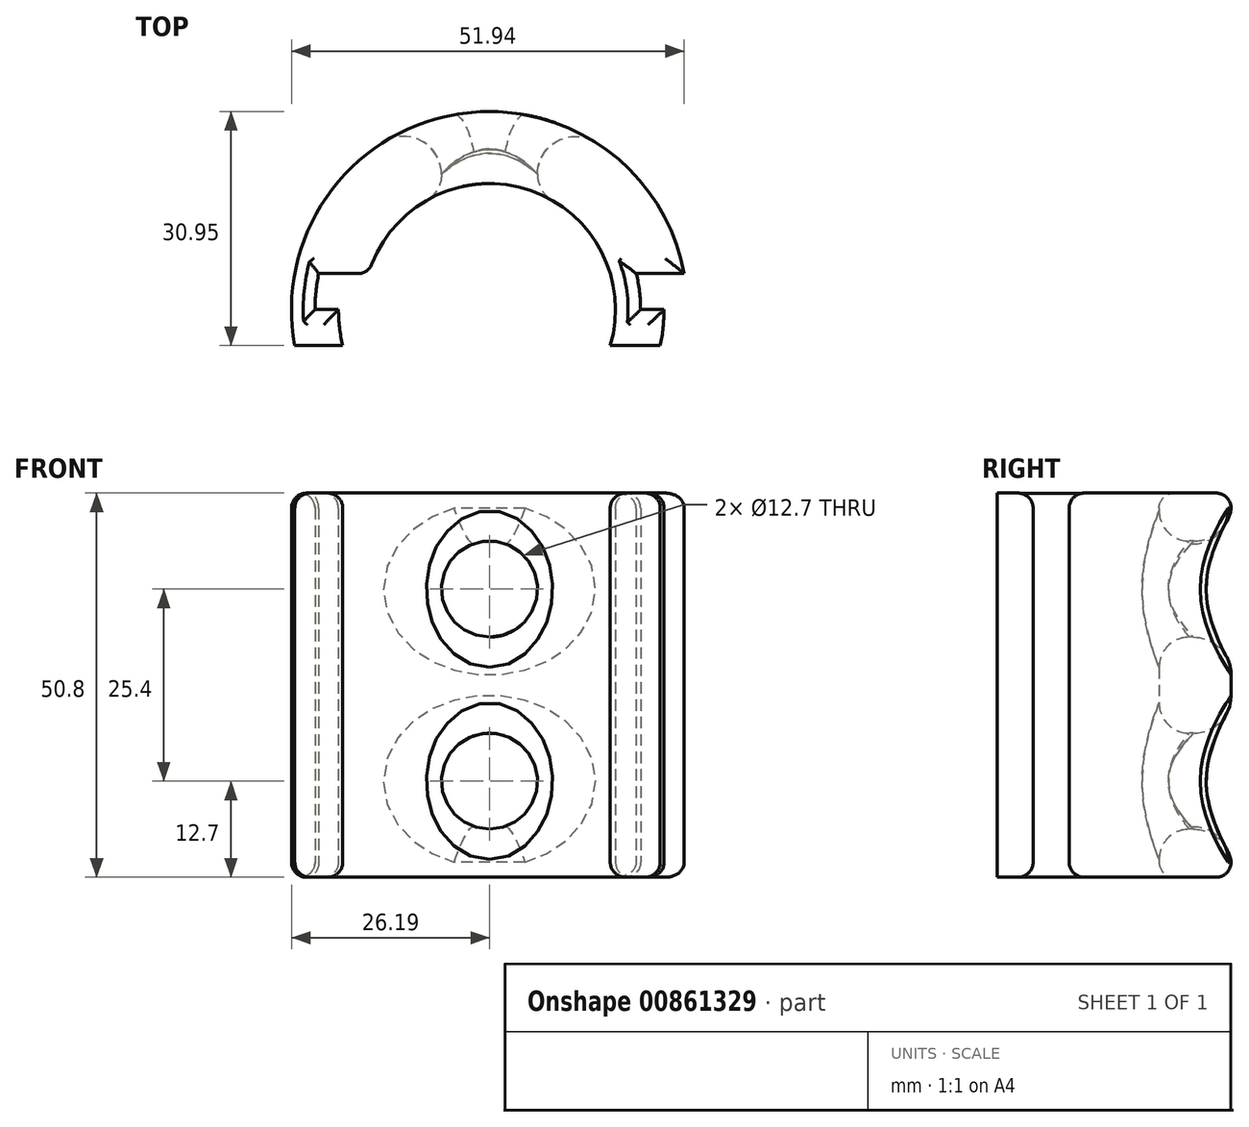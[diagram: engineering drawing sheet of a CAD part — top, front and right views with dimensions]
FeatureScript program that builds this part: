
annotation { "Feature Type Name" : "Feature", "Feature Type Description" : "" }
export const myFeature = defineFeature(function(context is Context, id is Id, definition is map)
    precondition{}
    {
        {
            var Q0;
            Q0=qCreatedBy(makeId("Top.planeOp"),FACE);
            var sketch = newSketch(context, id + "F0", { "sketchPlane" : qUnion([Q0])});
            skArc(sketch, "E0", {"start": v(15.96, -4.76) * mm, "mid": v(4.76, 15.96) * mm, "end": v(-15.96, 4.76) * mm});
            skArc(sketch, "E1", {"start": v(25.75, 4.76) * mm, "mid": v(-4.76, 25.75) * mm, "end": v(-25.75, -4.76) * mm});
            skLineSegment(sketch, "E2.top", {"start": v(-25.75, -4.76) * mm, "end": v(-19.4, -4.76) * mm, "construction": true});
            skLineSegment(sketch, "E3", {"start": v(-25.75, -4.76) * mm, "end": v(-19.4, -4.76) * mm});
            skArc(sketch, "E4", {"start": v(-19.97, 0) * mm, "mid": v(-19.83, -2.4) * mm, "end": v(-19.4, -4.76) * mm});
            skLineSegment(sketch, "E5", {"start": v(-25.75, -4.76) * mm, "end": v(-22.57, -4.76) * mm, "construction": true});
            skArc(sketch, "E6", {"start": v(22.57, -4.76) * mm, "mid": v(22.95, -2.4) * mm, "end": v(23.07, 0) * mm});
            skLineSegment(sketch, "E7", {"start": v(-19.97, 0) * mm, "end": v(-23.07, 0) * mm});
            skLineSegment(sketch, "E8", {"start": v(-22.57, 4.76) * mm, "end": v(-15.96, 4.76) * mm});
            skArc(sketch, "E9.trimOffspring", {"start": v(-22.57, 4.76) * mm, "mid": v(-22.95, 2.4) * mm, "end": v(-23.07, 0) * mm});
            skArc(sketch, "E10.trimOffspring", {"start": v(19.97, 0) * mm, "mid": v(19.83, 2.4) * mm, "end": v(19.4, 4.76) * mm});
            skLineSegment(sketch, "E11", {"start": v(15.96, -4.76) * mm, "end": v(22.57, -4.76) * mm});
            skLineSegment(sketch, "E12", {"start": v(23.07, 0) * mm, "end": v(19.97, 0) * mm});
            skLineSegment(sketch, "E13", {"start": v(19.4, 4.76) * mm, "end": v(25.75, 4.76) * mm});
            skLineSegment(sketch, "E14.trimOffspring", {"start": v(15.96, -4.76) * mm, "end": v(22.57, -4.76) * mm, "construction": true});
            skLineSegment(sketch, "E15.trimOffspring", {"start": v(19.4, 4.76) * mm, "end": v(25.75, 4.76) * mm, "construction": true});
            skLineSegment(sketch, "E16.trimOffspring", {"start": v(-22.57, 4.76) * mm, "end": v(-15.96, 4.76) * mm, "construction": true});
            skSolve(sketch);
        }
        {
            var Q0;
            Q0=makeQuery(id+"F0.imprint","IMPRINT",FACE,{"disambiguationData":[TD([[makeQuery(id+"F0.imprint","IMPRINT",EDGE,{"derivedFrom":sQuery(id+"F0.wireOp",EDGE,"E0")}),-1.0]])]});
            extrude(context, id + "F1", {"entities" : qUnion([Q0]), "depth" : 50.8 * mm, "offsetDistance" : 25 * mm});
        }
        {
            var Q0;
            Q0=qCreatedBy(makeId("Front.planeOp"),FACE);
            var sketch = newSketch(context, id + "F2", { "sketchPlane" : qUnion([Q0])});
            skLineSegment(sketch, "E17", {"start": v(0, 0) * mm, "end": v(0, 12.7) * mm, "construction": true});
            skLineSegment(sketch, "E18", {"start": v(0, 12.7) * mm, "end": v(0, 38.1) * mm, "construction": true});
            skCircle(sketch, "E19", {"center": v(0, 12.7) * mm, "radius": 6.35 * mm});
            skCircle(sketch, "E20", {"center": v(0, 38.1) * mm, "radius": 6.35 * mm});
            skSolve(sketch);
        }
        {
            var Q0;
            Q0=makeQuery(id+"F2.imprint","IMPRINT",FACE,{"disambiguationData":[TD([[makeQuery(id+"F2.imprint","IMPRINT",EDGE,{"derivedFrom":sQuery(id+"F2.wireOp",EDGE,"E20")}),1.0]])]});
            var Q1;
            Q1=makeQuery(id+"F2.imprint","IMPRINT",FACE,{"disambiguationData":[TD([[makeQuery(id+"F2.imprint","IMPRINT",EDGE,{"derivedFrom":sQuery(id+"F2.wireOp",EDGE,"E19")}),1.0]])]});
            extrude(context, id + "F3", {"entities" : qUnion([Q0, Q1]), "operationType" : NewBodyOperationType.REMOVE, "endBound" : BoundingType.THROUGH_ALL, "oppositeDirection" : true, "depth" : 25 * mm, "offsetDistance" : 25 * mm});
        }
        {
            var Q0;
            Q0=makeQuery(id+"F1.opExtrude","CAP_EDGE",EDGE,{"disambiguationData":[OSD([sQuery(id+"F0.wireOp",EDGE,"E1")])],"isStart":false});
            var Q1;
            Q1=makeQuery(id+"F1.opExtrude","CAP_EDGE",EDGE,{"disambiguationData":[OSD([sQuery(id+"F0.wireOp",EDGE,"E6")])],"isStart":false});
            var Q2;
            Q2=makeQuery(id+"F1.opExtrude","CAP_EDGE",EDGE,{"disambiguationData":[OSD([sQuery(id+"F0.wireOp",EDGE,"E13")])],"isStart":false});
            var Q3;
            Q3=makeQuery(id+"F1.opExtrude","CAP_EDGE",EDGE,{"disambiguationData":[OSD([sQuery(id+"F0.wireOp",EDGE,"E10.trimOffspring")])],"isStart":false});
            var Q4;
            Q4=makeQuery(id+"F1.opExtrude","CAP_EDGE",EDGE,{"disambiguationData":[OSD([sQuery(id+"F0.wireOp",EDGE,"E0")])],"isStart":false});
            var Q5;
            Q5=makeQuery(id+"F1.opExtrude","CAP_EDGE",EDGE,{"disambiguationData":[OSD([sQuery(id+"F0.wireOp",EDGE,"E8")])],"isStart":false});
            var Q6;
            Q6=makeQuery(id+"F1.opExtrude","CAP_EDGE",EDGE,{"disambiguationData":[OSD([sQuery(id+"F0.wireOp",EDGE,"E9.trimOffspring")])],"isStart":false});
            var Q7;
            Q7=makeQuery(id+"F1.opExtrude","CAP_EDGE",EDGE,{"disambiguationData":[OSD([sQuery(id+"F0.wireOp",EDGE,"E7")])],"isStart":false});
            var Q8;
            Q8=makeQuery(id+"F1.opExtrude","CAP_EDGE",EDGE,{"disambiguationData":[OSD([sQuery(id+"F0.wireOp",EDGE,"E12")])],"isStart":false});
            var Q9;
            Q9=makeQuery(id+"F1.opExtrude","CAP_EDGE",EDGE,{"disambiguationData":[OSD([sQuery(id+"F0.wireOp",EDGE,"E4")])],"isStart":false});
            var Q10;
            Q10=makeQuery(id+"F1.opExtrude","CAP_EDGE",EDGE,{"disambiguationData":[OSD([sQuery(id+"F0.wireOp",EDGE,"E0")])],"isStart":true});
            var Q11;
            Q11=makeQuery(id+"F1.opExtrude","CAP_EDGE",EDGE,{"disambiguationData":[OSD([sQuery(id+"F0.wireOp",EDGE,"E1")])],"isStart":true});
            var Q12;
            Q12=makeQuery(id+"F1.opExtrude","CAP_EDGE",EDGE,{"disambiguationData":[OSD([sQuery(id+"F0.wireOp",EDGE,"E13")])],"isStart":true});
            var Q13;
            Q13=makeQuery(id+"F1.opExtrude","CAP_EDGE",EDGE,{"disambiguationData":[OSD([sQuery(id+"F0.wireOp",EDGE,"E12")])],"isStart":true});
            var Q14;
            Q14=makeQuery(id+"F1.opExtrude","CAP_EDGE",EDGE,{"disambiguationData":[OSD([sQuery(id+"F0.wireOp",EDGE,"E6")])],"isStart":true});
            var Q15;
            Q15=makeQuery(id+"F1.opExtrude","CAP_EDGE",EDGE,{"disambiguationData":[OSD([sQuery(id+"F0.wireOp",EDGE,"E4")])],"isStart":true});
            var Q16;
            Q16=makeQuery(id+"F1.opExtrude","CAP_EDGE",EDGE,{"disambiguationData":[OSD([sQuery(id+"F0.wireOp",EDGE,"E8")])],"isStart":true});
            var Q17;
            Q17=makeQuery(id+"F1.opExtrude","CAP_EDGE",EDGE,{"disambiguationData":[OSD([sQuery(id+"F0.wireOp",EDGE,"E10.trimOffspring")])],"isStart":true});
            var Q18;
            Q18=makeQuery(id+"F1.opExtrude","CAP_EDGE",EDGE,{"disambiguationData":[OSD([sQuery(id+"F0.wireOp",EDGE,"E9.trimOffspring")])],"isStart":true});
            var Q19;
            Q19=makeQuery(id+"F1.opExtrude","CAP_EDGE",EDGE,{"disambiguationData":[OSD([sQuery(id+"F0.wireOp",EDGE,"E7")])],"isStart":true});
            var Q20;
            Q20=makeQuery(id+"F1.opExtrude","SWEPT_EDGE",EDGE,{"disambiguationData":[OSD([sQuery(id+"F0.wireOp",EDGE,"E0"),sQuery(id+"F0.wireOp",EDGE,"E8")])]});
            fillet(context, id + "F4", {"entities" : qUnion([Q0, Q1, Q2, Q3, Q4, Q5, Q6, Q7, Q8, Q9, Q10, Q11, Q12, Q13, Q14, Q15, Q16, Q17, Q18, Q19, Q20]), "radius" : 2 * mm, "tangentPropagation" : true, "allowEdgeOverflow" : false});
        }
        {
            var Q0;
            Q0=makeQuery(id+"F3.boolean.opBoolean","INTERSECT",EDGE,{"derivedFrom":[makeQuery(id+"F1.opExtrude","SWEPT_FACE",FACE,{"disambiguationData":[OSD([sQuery(id+"F0.wireOp",EDGE,"E1")])]}),makeQuery(id+"F3.opExtrude","SWEPT_FACE",FACE,{"disambiguationData":[OSD([sQuery(id+"F2.wireOp",EDGE,"E20")])]})]});
            var Q1;
            Q1=makeQuery(id+"F3.boolean.opBoolean","INTERSECT",EDGE,{"derivedFrom":[makeQuery(id+"F1.opExtrude","SWEPT_FACE",FACE,{"disambiguationData":[OSD([sQuery(id+"F0.wireOp",EDGE,"E1")])]}),makeQuery(id+"F3.opExtrude","SWEPT_FACE",FACE,{"disambiguationData":[OSD([sQuery(id+"F2.wireOp",EDGE,"E19")])]})]});
            fillet(context, id + "F5", {"entities" : qUnion([Q0, Q1]), "radius" : 5 * mm, "tangentPropagation" : true, "allowEdgeOverflow" : false});
        }
        {
            var Q0;
            Q0=makeQuery(id+"F3.boolean.opBoolean","INTERSECT",EDGE,{"derivedFrom":[makeQuery(id+"F1.opExtrude","SWEPT_FACE",FACE,{"disambiguationData":[OSD([sQuery(id+"F0.wireOp",EDGE,"E0")])]}),makeQuery(id+"F3.opExtrude","SWEPT_FACE",FACE,{"disambiguationData":[OSD([sQuery(id+"F2.wireOp",EDGE,"E19")])]})]});
            var Q1;
            Q1=makeQuery(id+"F3.boolean.opBoolean","INTERSECT",EDGE,{"derivedFrom":[makeQuery(id+"F1.opExtrude","SWEPT_FACE",FACE,{"disambiguationData":[OSD([sQuery(id+"F0.wireOp",EDGE,"E0")])]}),makeQuery(id+"F3.opExtrude","SWEPT_FACE",FACE,{"disambiguationData":[OSD([sQuery(id+"F2.wireOp",EDGE,"E20")])]})]});
            fillet(context, id + "F6", {"entities" : qUnion([Q0, Q1]), "radius" : 4 * mm, "tangentPropagation" : true, "allowEdgeOverflow" : false});
        }
    });
